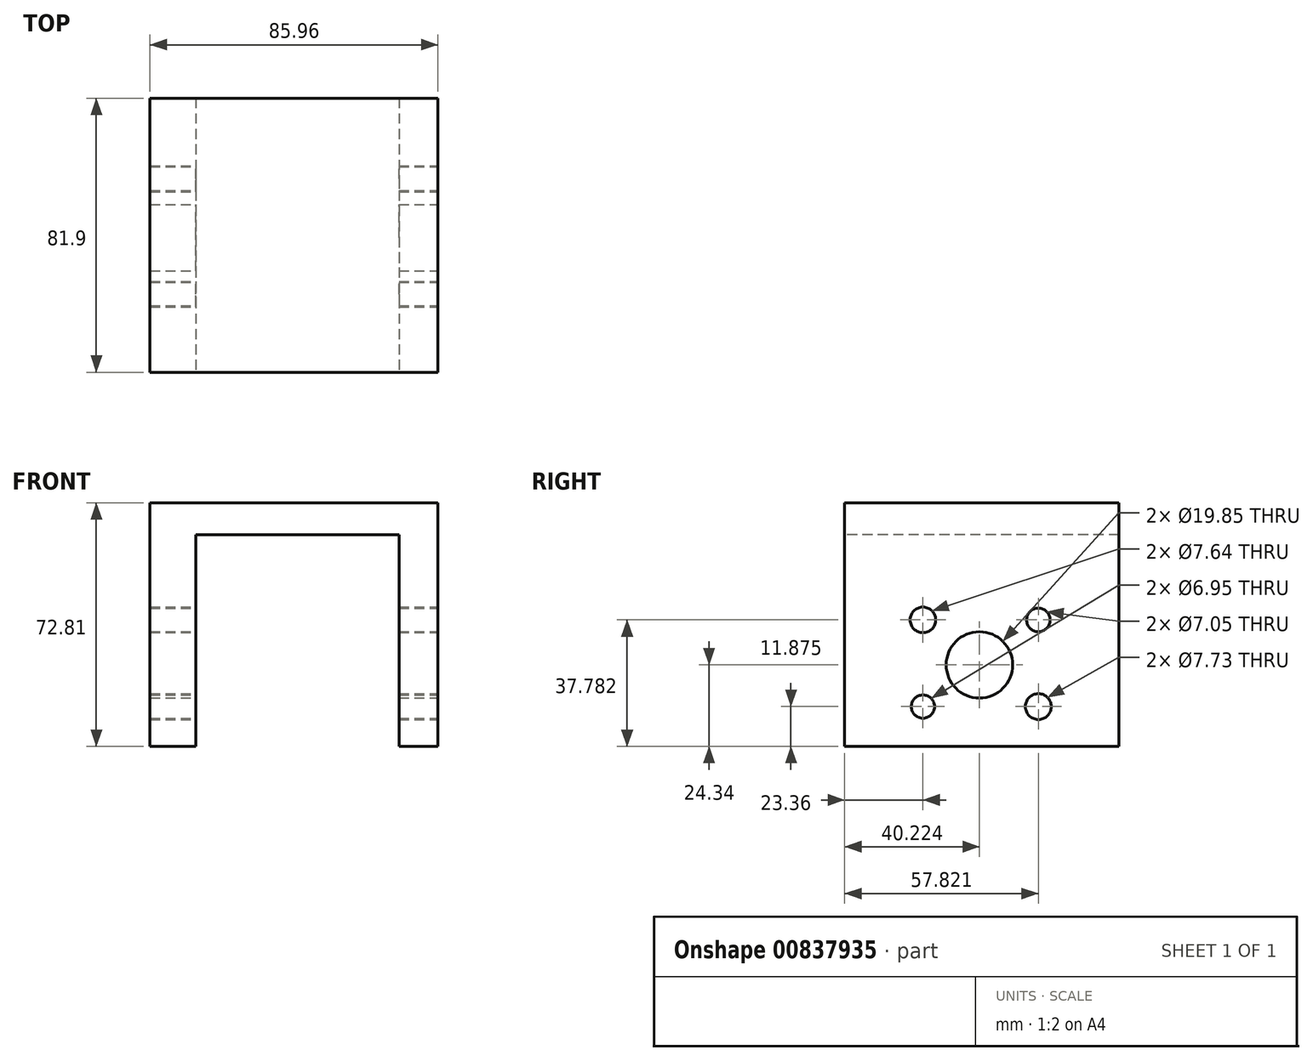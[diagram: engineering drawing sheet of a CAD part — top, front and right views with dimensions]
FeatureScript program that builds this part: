
annotation { "Feature Type Name" : "Feature", "Feature Type Description" : "" }
export const myFeature = defineFeature(function(context is Context, id is Id, definition is map)
    precondition{}
    {
        {
            var Q0;
            Q0=qCreatedBy(makeId("Front.planeOp"),FACE);
            var sketch = newSketch(context, id + "F0", { "sketchPlane" : qUnion([Q0])});
            skLineSegment(sketch, "E0.bottom", {"start": v(-43.49, 31.6) * mm, "end": v(42.47, 31.6) * mm});
            skLineSegment(sketch, "E0.top", {"start": v(-43.49, -41.21) * mm, "end": v(-29.83, -41.21) * mm});
            skLineSegment(sketch, "E0.left", {"start": v(-43.49, 31.6) * mm, "end": v(-43.49, -41.21) * mm});
            skLineSegment(sketch, "E0.right", {"start": v(42.47, 31.6) * mm, "end": v(42.47, -41.21) * mm});
            skLineSegment(sketch, "E1.bottom", {"start": v(-29.83, 22) * mm, "end": v(30.84, 22) * mm});
            skLineSegment(sketch, "E1.left", {"start": v(-29.83, 22) * mm, "end": v(-29.83, -41.21) * mm});
            skLineSegment(sketch, "E1.right", {"start": v(30.84, 22) * mm, "end": v(30.84, -41.21) * mm});
            skLineSegment(sketch, "E2.trimOffspring", {"start": v(30.84, -41.21) * mm, "end": v(42.47, -41.21) * mm});
            skSolve(sketch);
        }
        {
            var Q0;
            Q0=makeQuery(id+"F0.imprint","IMPRINT",FACE,{"disambiguationData":[TD([[makeQuery(id+"F0.imprint","IMPRINT",EDGE,{"derivedFrom":sQuery(id+"F0.wireOp",EDGE,"E0.bottom")}),-1.0]])]});
            extrude(context, id + "F1", {"entities" : qUnion([Q0]), "oppositeDirection" : true, "depth" : 81.9 * mm, "offsetDistance" : 25 * mm});
        }
        {
            var Q0;
            Q0=makeQuery(id+"F1.opExtrude","SWEPT_FACE",FACE,{"disambiguationData":[OSD([sQuery(id+"F0.wireOp",EDGE,"E0.right")])]});
            var sketch = newSketch(context, id + "F2", { "sketchPlane" : qUnion([Q0])});
            skCircle(sketch, "E3", {"center": v(40.22, -16.87) * mm, "radius": 9.92 * mm});
            skCircle(sketch, "E4", {"center": v(23.36, -3.43) * mm, "radius": 3.82 * mm});
            skCircle(sketch, "E5", {"center": v(23.36, -29.33) * mm, "radius": 3.47 * mm});
            skCircle(sketch, "E6", {"center": v(57.82, -3.43) * mm, "radius": 3.52 * mm});
            skCircle(sketch, "E7", {"center": v(57.82, -29.33) * mm, "radius": 3.86 * mm});
            skSolve(sketch);
        }
        {
            var Q0;
            Q0 = qSketchRegion(id + "F2", true);
            extrude(context, id + "F3", {"entities" : qUnion([Q0]), "operationType" : NewBodyOperationType.REMOVE, "oppositeDirection" : true, "depth" : 140.3 * mm, "offsetDistance" : 25 * mm});
        }
    });
